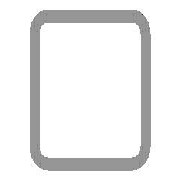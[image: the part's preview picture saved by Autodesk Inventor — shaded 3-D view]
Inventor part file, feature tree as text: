
AUTODESK INVENTOR PART (.ipt)
format: ipt  version: 2025.1 (Build 291241020, 241B)  size: 141,824 bytes
history: native  units: mm (DEFAULTED — no unit token found)
features: other x4, sketch x1, plane x1
ambient origin geometry x8: Origin, YZ Plane, XZ Plane, XY Plane, X Axis, Y Axis, Z Axis, Center Point
bodies: Solid1 (feature_tree), Body (feature_tree)
feature tree (6):
  parser-record x1  (decoder bookkeeping rows leaked as tree rows — omitted from the tree; the rows remain in map.json)
  other  "Driven Length"
  other  "Start Plane"
  other  "End Plane"
  sketch  "Sketch3"  dims[d3=530.0mm d4=0.0mm d7=4.0mm d9=40.0mm d11=40.0mm d12=2.0mm d13=50.0mm d14=580.0mm d15=20.0mm d16=20.0mm d17=90.0deg d18=530.0mm]
  plane  "Work Plane3"
